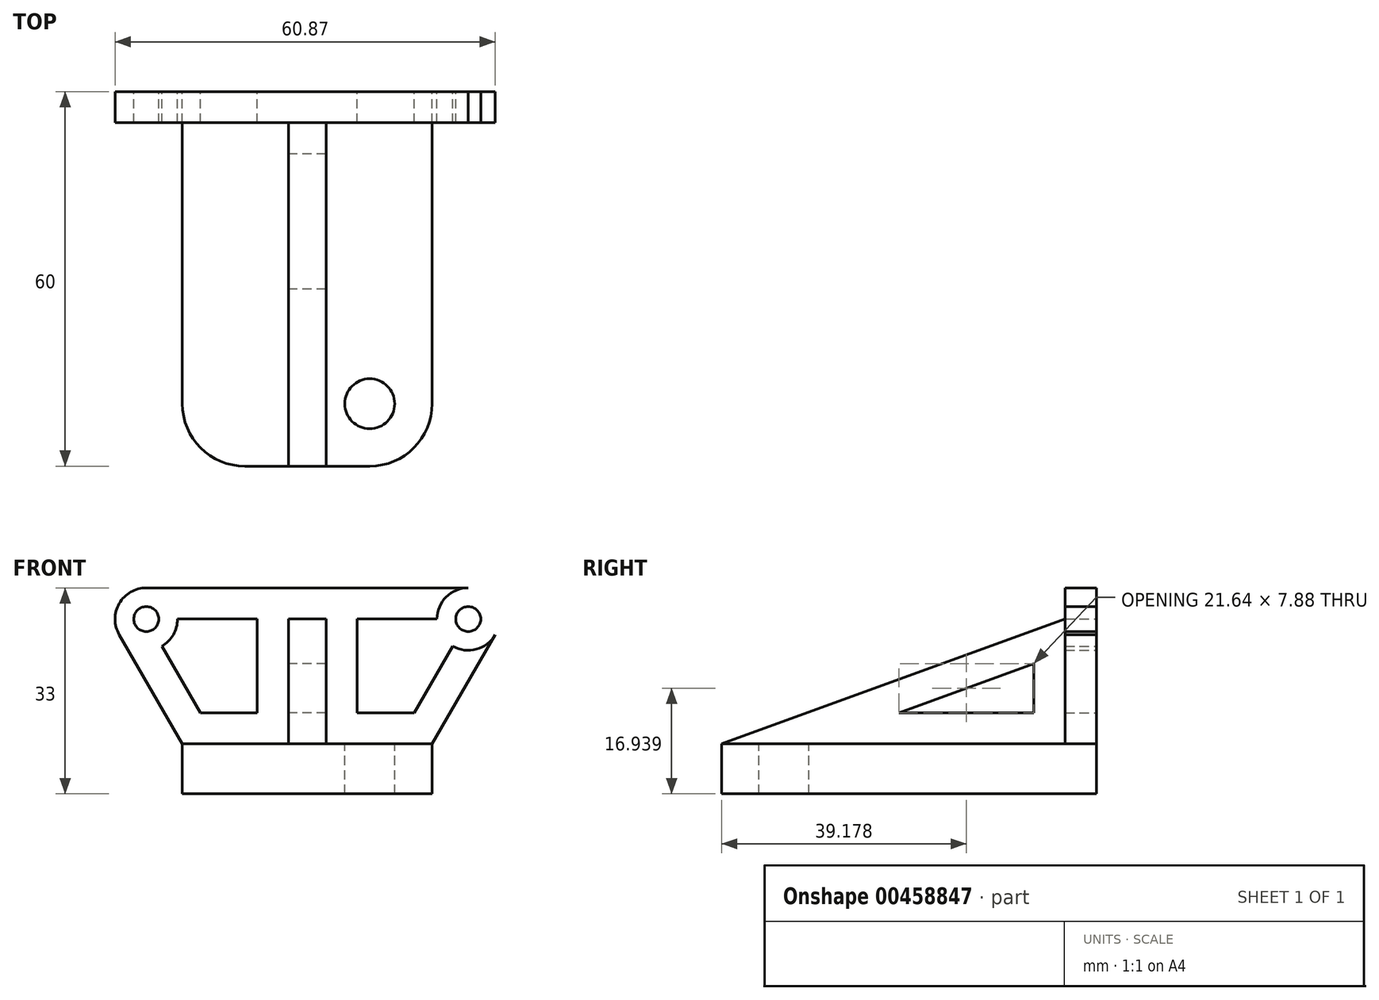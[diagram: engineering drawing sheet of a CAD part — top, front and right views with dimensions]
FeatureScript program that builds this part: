
annotation { "Feature Type Name" : "Feature", "Feature Type Description" : "" }
export const myFeature = defineFeature(function(context is Context, id is Id, definition is map)
    precondition{}
    {
        {
            var Q0;
            Q0=qCreatedBy(makeId("Front.planeOp"),FACE);
            var sketch = newSketch(context, id + "F0", { "sketchPlane" : qUnion([Q0])});
            skLineSegment(sketch, "E0.bottom", {"start": v(0, 0) * mm, "end": v(-20, 0) * mm});
            skLineSegment(sketch, "E0.top", {"start": v(0, -8) * mm, "end": v(-20, -8) * mm});
            skLineSegment(sketch, "E0.left", {"start": v(0, 0) * mm, "end": v(0, -8) * mm});
            skLineSegment(sketch, "E0.right", {"start": v(-20, 0) * mm, "end": v(-20, -8) * mm});
            skLineSegment(sketch, "E1", {"start": v(-20, 0) * mm, "end": v(-30.1, 17.5) * mm});
            skLineSegment(sketch, "E2", {"start": v(0, -8) * mm, "end": v(0, 25) * mm, "construction": true});
            skPoint(sketch, "E2.endSnap0", {"position": v(0, -4) * mm});
            skCircle(sketch, "E3", {"center": v(-25.77, 20) * mm, "radius": 5 * mm});
            skPoint(sketch, "E3.second.point", {"position": v(-20.77, 20) * mm});
            skPoint(sketch, "E3.third.point", {"position": v(-25.77, 25) * mm});
            skCircle(sketch, "E4", {"center": v(-25.77, 20) * mm, "radius": 2 * mm});
            skLineSegment(sketch, "E5", {"start": v(-25.77, 25) * mm, "end": v(0, 25) * mm});
            skLineSegment(sketch, "E6", {"start": v(-23.27, 15.67) * mm, "end": v(-17.11, 5) * mm});
            skLineSegment(sketch, "E7", {"start": v(-20.77, 20) * mm, "end": v(-8, 20) * mm});
            skLineSegment(sketch, "E8", {"start": v(-8, 20) * mm, "end": v(-8, 5) * mm});
            skLineSegment(sketch, "E9", {"start": v(-8, 5) * mm, "end": v(-17.11, 5) * mm});
            skLineSegment(sketch, "E10", {"start": v(-3, 20) * mm, "end": v(-3, 0) * mm});
            skLineSegment(sketch, "E11", {"start": v(-3, 20) * mm, "end": v(0, 20) * mm});
            skLineSegment(sketch, "E12.MirrorCS", {"start": v(25.77, 25) * mm, "end": v(0, 25) * mm});
            skCircle(sketch, "E13.MirrorC", {"center": v(25.77, 20) * mm, "radius": 5 * mm});
            skCircle(sketch, "E14.MirrorC", {"center": v(25.77, 20) * mm, "radius": 2 * mm});
            skLineSegment(sketch, "E15.MirrorCS", {"start": v(20, 0) * mm, "end": v(30.1, 17.5) * mm});
            skLineSegment(sketch, "E16.MirrorCS", {"start": v(23.27, 15.67) * mm, "end": v(17.11, 5) * mm});
            skLineSegment(sketch, "E17.MirrorCS", {"start": v(8, 5) * mm, "end": v(17.11, 5) * mm});
            skLineSegment(sketch, "E18.MirrorCS", {"start": v(8, 20) * mm, "end": v(8, 5) * mm});
            skLineSegment(sketch, "E19.MirrorCS", {"start": v(20.77, 20) * mm, "end": v(8, 20) * mm});
            skLineSegment(sketch, "E20.MirrorCS", {"start": v(3, 20) * mm, "end": v(3, 0) * mm});
            skLineSegment(sketch, "E21.MirrorCS", {"start": v(3, 20) * mm, "end": v(0, 20) * mm});
            skLineSegment(sketch, "E22.MirrorCS", {"start": v(0, -8) * mm, "end": v(20, -8) * mm});
            skLineSegment(sketch, "E23.MirrorCS", {"start": v(0, 0) * mm, "end": v(20, 0) * mm});
            skLineSegment(sketch, "E24.MirrorCS", {"start": v(20, 0) * mm, "end": v(20, -8) * mm});
            skSolve(sketch);
        }
        {
            var Q0;
            {var subQ3=sQuery(id+"F0.wireOp",EDGE,"E1");Q0=makeQuery(id+"F0.imprint","IMPRINT",FACE,{"disambiguationData":[TD([[makeQuery(id+"F0.imprint","IMPRINT",EDGE,{"derivedFrom":subQ3}),-1.0]])]});}
            var Q1;
            Q1=makeQuery(id+"F0.imprint","IMPRINT",FACE,{"disambiguationData":[TD([[makeQuery(id+"F0.imprint","IMPRINT",EDGE,{"derivedFrom":sQuery(id+"F0.wireOp",EDGE,"E4")}),-1.0]])]});
            var Q2;
            Q2=makeQuery(id+"F0.imprint","IMPRINT",FACE,{"disambiguationData":[TD([[makeQuery(id+"F0.imprint","IMPRINT",EDGE,{"derivedFrom":sQuery(id+"F0.wireOp",EDGE,"E14.MirrorC")}),1.0]])]});
            extrude(context, id + "F1", {"entities" : qUnion([Q0, Q1, Q2]), "depth" : 5 * mm});
        }
        {
            var Q0;
            {var subQ1=sQuery(id+"F0.wireOp",EDGE,"E0.left");Q0=makeQuery(id+"F0.imprint","IMPRINT",FACE,{"disambiguationData":[TD([[makeQuery(id+"F0.imprint","IMPRINT",EDGE,{"derivedFrom":subQ1}),1.0]])]});}
            var Q1;
            Q1=makeQuery(id+"F0.imprint","IMPRINT",FACE,{"disambiguationData":[TD([[makeQuery(id+"F0.imprint","IMPRINT",EDGE,{"derivedFrom":sQuery(id+"F0.wireOp",EDGE,"E0.top")}),-1.0]])]});
            extrude(context, id + "F2", {"entities" : qUnion([Q0, Q1]), "depth" : 60 * mm});
        }
        {
            var Q0;
            Q0=qCreatedBy(makeId("Right.planeOp"),FACE);
            var sketch = newSketch(context, id + "F3", { "sketchPlane" : qUnion([Q0])});
            skLineSegment(sketch, "E25", {"start": v(-60, 0) * mm, "end": v(0, 0) * mm});
            skLineSegment(sketch, "E26", {"start": v(0, 0) * mm, "end": v(0, 21.84) * mm});
            skLineSegment(sketch, "E27", {"start": v(0, 21.84) * mm, "end": v(-60, 0) * mm});
            skLineSegment(sketch, "E28.0", {"start": v(-10, 12.88) * mm, "end": v(-31.64, 5) * mm});
            skLineSegment(sketch, "E28.1", {"start": v(-10, 5) * mm, "end": v(-10, 12.88) * mm});
            skLineSegment(sketch, "E28.2", {"start": v(-31.64, 5) * mm, "end": v(-10, 5) * mm});
            skSolve(sketch);
        }
        {
            var Q0;
            Q0 = qSketchRegion(id + "F3", true);
            extrude(context, id + "F4", {"entities" : qUnion([Q0]), "operationType" : NewBodyOperationType.ADD, "depth" : 6 * mm, "symmetric" : true});
        }
        {
            var Q0;
            Q0=qCreatedBy(makeId("Top.planeOp"),FACE);
            var sketch = newSketch(context, id + "F5", { "sketchPlane" : qUnion([Q0])});
            skCircle(sketch, "E29", {"center": v(10, -50) * mm, "radius": 4 * mm});
            skCircle(sketch, "E30.MirrorC", {"center": v(-10, -50) * mm, "radius": 4 * mm});
            skSolve(sketch);
        }
        {
            var Q0;
            Q0=makeQuery(id+"F5.imprint","IMPRINT",FACE,{"disambiguationData":[TD([[makeQuery(id+"F5.imprint","IMPRINT",EDGE,{"derivedFrom":sQuery(id+"F5.wireOp",EDGE,"E30.MirrorC")}),-1.0]])]});
            var Q1;
            Q1=makeQuery(id+"F5.imprint","IMPRINT",FACE,{"disambiguationData":[TD([[makeQuery(id+"F5.imprint","IMPRINT",EDGE,{"derivedFrom":sQuery(id+"F5.wireOp",EDGE,"E29")}),1.0]])]});
            extrude(context, id + "F6", {"entities" : qUnion([Q0, Q1]), "operationType" : NewBodyOperationType.REMOVE, "endBound" : BoundingType.THROUGH_ALL, "oppositeDirection" : true, "depth" : 25 * mm});
        }
        {
            var Q0;
            Q0=makeQuery(id+"F2.opExtrude","CAP_EDGE",EDGE,{"disambiguationData":[OSD([sQuery(id+"F0.wireOp",EDGE,"E0.right")])],"isStart":false});
            var Q1;
            Q1=makeQuery(id+"F2.opExtrude","CAP_EDGE",EDGE,{"disambiguationData":[OSD([sQuery(id+"F0.wireOp",EDGE,"E24.MirrorCS")])],"isStart":false});
            fillet(context, id + "F7", {"entities" : qUnion([Q0, Q1]), "radius" : 10 * mm, "tangentPropagation" : true, "allowEdgeOverflow" : false});
        }
    });
